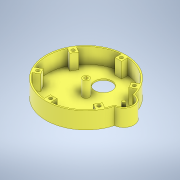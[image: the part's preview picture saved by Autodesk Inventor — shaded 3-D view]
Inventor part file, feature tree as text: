
AUTODESK INVENTOR PART (.ipt)
format: ipt  version: 2022.1 (Build 261234020, 234B)  size: 290,304 bytes
history: native  units: in
note: dims shown in document units (in); Inventor stores cm internally (conversion verified against a paired STEP export)
features: sketch x11, extrude x8, hole x2, revolve x1, pattern_circular x1
ambient origin geometry x8: Origin, YZ Plane, XZ Plane, XY Plane, X Axis, Y Axis, Z Axis, Center Point
bodies: Body1 (feature_tree)
feature tree (23):
  revolve  "Revolution1"  [1 undecoded]
  extrude  "Extrusion2"  TaperAngle=90.0deg  [1 undecoded]
  extrude  "HoleForTelescopeInsert"  Depth=1.15in
  hole  "Hole1"  [1 undecoded]
  extrude  "Extrusion5"  TaperAngle=0.0deg  [1 undecoded]
  hole  "Hole4"  [1 undecoded]
  pattern_circular  "Circular Pattern1"  Count=6 Angle=360.0deg
  extrude  "Extrusion6"  Depth=0.375in
  extrude  "Extrusion7"  Depth=0.375in
  extrude  "Extrusion8"  Depth=1.15in TaperAngle=0.0deg
  extrude  "Extrusion9"  Depth=0.375in
  extrude  "Extrusion10"  Depth=2.825in
  sketch  "Sketch3"  dims[d3=3.0in d4=1.25in]
  sketch  "Sketch4"  dims[d5=0.1in d7=90.0deg]
  sketch  "Sketch5"  dims[d8=0.49in d9=1.15in]
  sketch  "Sketch6"  dims[d10=0.0in d11=1.3057in]
  sketch  "Sketch8"  dims[d12=1.28in d13=0.0in d14=0.0in]
  sketch  "Sketch10"  dims[d15=0.1in]
  sketch  "Sketch12"  dims[d16=0.249in d17=0.75in d18=0.257in d19=0.3in d20=0.5635in d21=0.575in d22=0.0in d27=4.85in]
  sketch  "Sketch13"  dims[d28=0.5in]
  sketch  "Sketch14"  dims[d29=1.15in d30=0.0in]
  sketch  "Sketch15"  dims[d45=0.218in d46=0.75in d47=0.249in d48=0.2422in d49=0.5635in d50=0.375in d51=0.0in d52=2.3622in d53=360.0deg]
  sketch  "Sketch16"  dims[d55=0.7in d56=0.0921in d58=0.7in d59=1.15in d60=0.0in d61=0.24in d62=2.825in d63=1.15in d64=0.0in d65=0.1in d66=1.25in d67=0.0in d68=1.0in d69=0.0in d70=1.0in d71=0.0in d23=1.0in d24=1.0in d25=1.0in d26=0.15in d31=0.8108in d32=0.0625in d33=0.75in d34=0.375in]
note: 5 required parameter values undecoded (feature->parameter linkage not recoverable at this tier; creation-order binding heuristic only, values carry confidence <= 0.55)